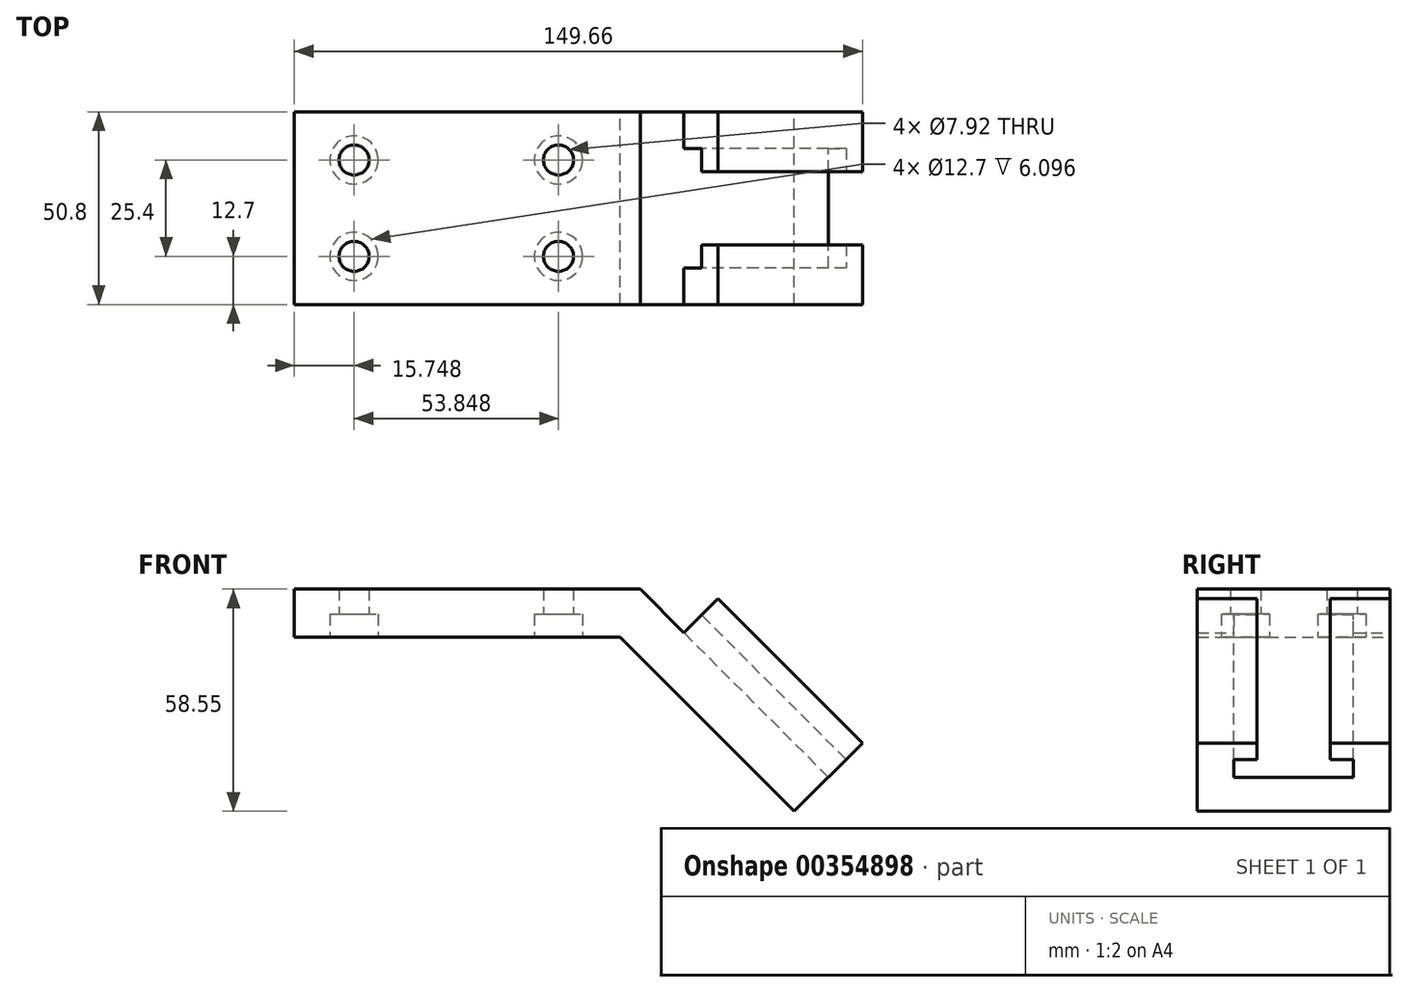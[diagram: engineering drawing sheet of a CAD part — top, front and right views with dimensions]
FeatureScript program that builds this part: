
annotation { "Feature Type Name" : "Feature", "Feature Type Description" : "" }
export const myFeature = defineFeature(function(context is Context, id is Id, definition is map)
    precondition{}
    {
        {
            var Q0;
            Q0=qCreatedBy(makeId("Front.planeOp"),FACE);
            var sketch = newSketch(context, id + "F0", { "sketchPlane" : qUnion([Q0])});
            skLineSegment(sketch, "E0", {"start": v(0, 0) * mm, "end": v(85.85, 0) * mm});
            skLineSegment(sketch, "E1", {"start": v(85.85, 0) * mm, "end": v(131.7, -45.85) * mm});
            skLineSegment(sketch, "E2", {"start": v(131.7, -45.85) * mm, "end": v(149.66, -27.9) * mm});
            skLineSegment(sketch, "E3", {"start": v(149.66, -27.9) * mm, "end": v(111.59, 10.19) * mm});
            skLineSegment(sketch, "E4", {"start": v(111.59, 10.19) * mm, "end": v(102.6, 1.2) * mm});
            skLineSegment(sketch, "E5", {"start": v(102.6, 1.2) * mm, "end": v(91.11, 12.7) * mm});
            skLineSegment(sketch, "E6", {"start": v(91.11, 12.7) * mm, "end": v(0, 12.7) * mm});
            skLineSegment(sketch, "E7", {"start": v(0, 12.7) * mm, "end": v(0, 0) * mm});
            skSolve(sketch);
        }
        {
            var Q0;
            Q0 = qSketchRegion(id + "F0", true);
            extrude(context, id + "F1", {"entities" : qUnion([Q0]), "depth" : 50.8 * mm});
        }
        {
            var Q0;
            Q0=makeQuery(id+"F1.opExtrude","SWEPT_FACE",FACE,{"disambiguationData":[OSD([sQuery(id+"F0.wireOp",EDGE,"E3")])]});
            var sketch = newSketch(context, id + "F2", { "sketchPlane" : qUnion([Q0])});
            skArc(sketch, "E8", {"start": v(119.18, -50.8) * mm, "mid": v(125.55, -25.4) * mm, "end": v(119.18, 0) * mm});
            skLineSegment(sketch, "E9", {"start": v(119.18, 0) * mm, "end": v(125.55, 0) * mm});
            skLineSegment(sketch, "E10", {"start": v(125.55, 0) * mm, "end": v(125.55, -50.8) * mm});
            skLineSegment(sketch, "E11", {"start": v(125.55, -50.8) * mm, "end": v(119.18, -50.8) * mm});
            skSolve(sketch);
        }
        {
            var Q0;
            Q0 = qSketchRegion(id + "F2", true);
            extrude(context, id + "F3", {"entities" : qUnion([Q0]), "operationType" : NewBodyOperationType.REMOVE, "oppositeDirection" : true, "depth" : 50.8 * mm});
        }
        {
            var Q0;
            Q0=makeQuery(id+"F1.opExtrude","SWEPT_FACE",FACE,{"disambiguationData":[OSD([sQuery(id+"F0.wireOp",EDGE,"E4")])]});
            var sketch = newSketch(context, id + "F4", { "sketchPlane" : qUnion([Q0])});
            skLineSegment(sketch, "E12", {"start": v(9.65, 73.4) * mm, "end": v(9.65, 80.01) * mm});
            skLineSegment(sketch, "E13", {"start": v(9.65, 80.01) * mm, "end": v(15.75, 80.01) * mm});
            skLineSegment(sketch, "E14", {"start": v(15.75, 80.01) * mm, "end": v(15.75, 86.1) * mm});
            skLineSegment(sketch, "E15", {"start": v(15.75, 86.1) * mm, "end": v(35.05, 86.1) * mm});
            skLineSegment(sketch, "E16", {"start": v(35.05, 86.1) * mm, "end": v(35.05, 80.01) * mm});
            skLineSegment(sketch, "E17", {"start": v(35.05, 80.01) * mm, "end": v(41.15, 80.01) * mm});
            skLineSegment(sketch, "E18", {"start": v(41.15, 80.01) * mm, "end": v(41.15, 73.4) * mm});
            skLineSegment(sketch, "E19", {"start": v(41.15, 73.4) * mm, "end": v(9.65, 73.4) * mm});
            skSolve(sketch);
        }
        {
            var Q0;
            Q0 = qSketchRegion(id + "F4", true);
            extrude(context, id + "F5", {"entities" : qUnion([Q0]), "operationType" : NewBodyOperationType.REMOVE, "oppositeDirection" : true, "depth" : 53.85 * mm});
        }
        {
            var Q0;
            Q0=makeQuery(id+"F1.opExtrude","SWEPT_FACE",FACE,{"disambiguationData":[OSD([sQuery(id+"F0.wireOp",EDGE,"E0")])]});
            var sketch = newSketch(context, id + "F6", { "sketchPlane" : qUnion([Q0])});
            skPoint(sketch, "E20", {"position": v(15.75, 38.1) * mm});
            skPoint(sketch, "E21", {"position": v(15.75, 12.7) * mm});
            skPoint(sketch, "E22", {"position": v(69.6, 12.7) * mm});
            skPoint(sketch, "E23", {"position": v(69.6, 38.1) * mm});
            skSolve(sketch);
        }
        {
            var Q0;
            Q0=sQuery(id+"F6.wireOp",VERTEX,"E20");
            var Q1;
            Q1=sQuery(id+"F6.wireOp",VERTEX,"E21");
            var Q2;
            Q2=sQuery(id+"F6.wireOp",VERTEX,"E22");
            var Q3;
            Q3=sQuery(id+"F6.wireOp",VERTEX,"E23");
            var Q4;
            Q4=makeQuery(id+"F1.opExtrude","SWEPT_BODY",BODY,{"disambiguationData":[OSD([sQuery(id+"F0.wireOp",EDGE,"E0"),sQuery(id+"F0.wireOp",EDGE,"E1"),sQuery(id+"F0.wireOp",EDGE,"E2"),sQuery(id+"F0.wireOp",EDGE,"E3"),sQuery(id+"F0.wireOp",EDGE,"E4"),sQuery(id+"F0.wireOp",EDGE,"E5"),sQuery(id+"F0.wireOp",EDGE,"E6"),sQuery(id+"F0.wireOp",EDGE,"E7")])]});
            hole(context, id + "F7", {"style" : HoleStyle.C_BORE, "endStyle" : HoleEndStyle.THROUGH, "holeDiameter" : 7.92 * mm, "cBoreDiameter" : 12.7 * mm, "cBoreDepth" : 6.1 * mm, "isTappedThrough" : true, "tappedDepth" : 12.7 * mm, "tapClearance" : 3, "locations" : qUnion([Q0, Q1, Q2, Q3]), "scope" : qUnion([Q4])});
        }
    });
